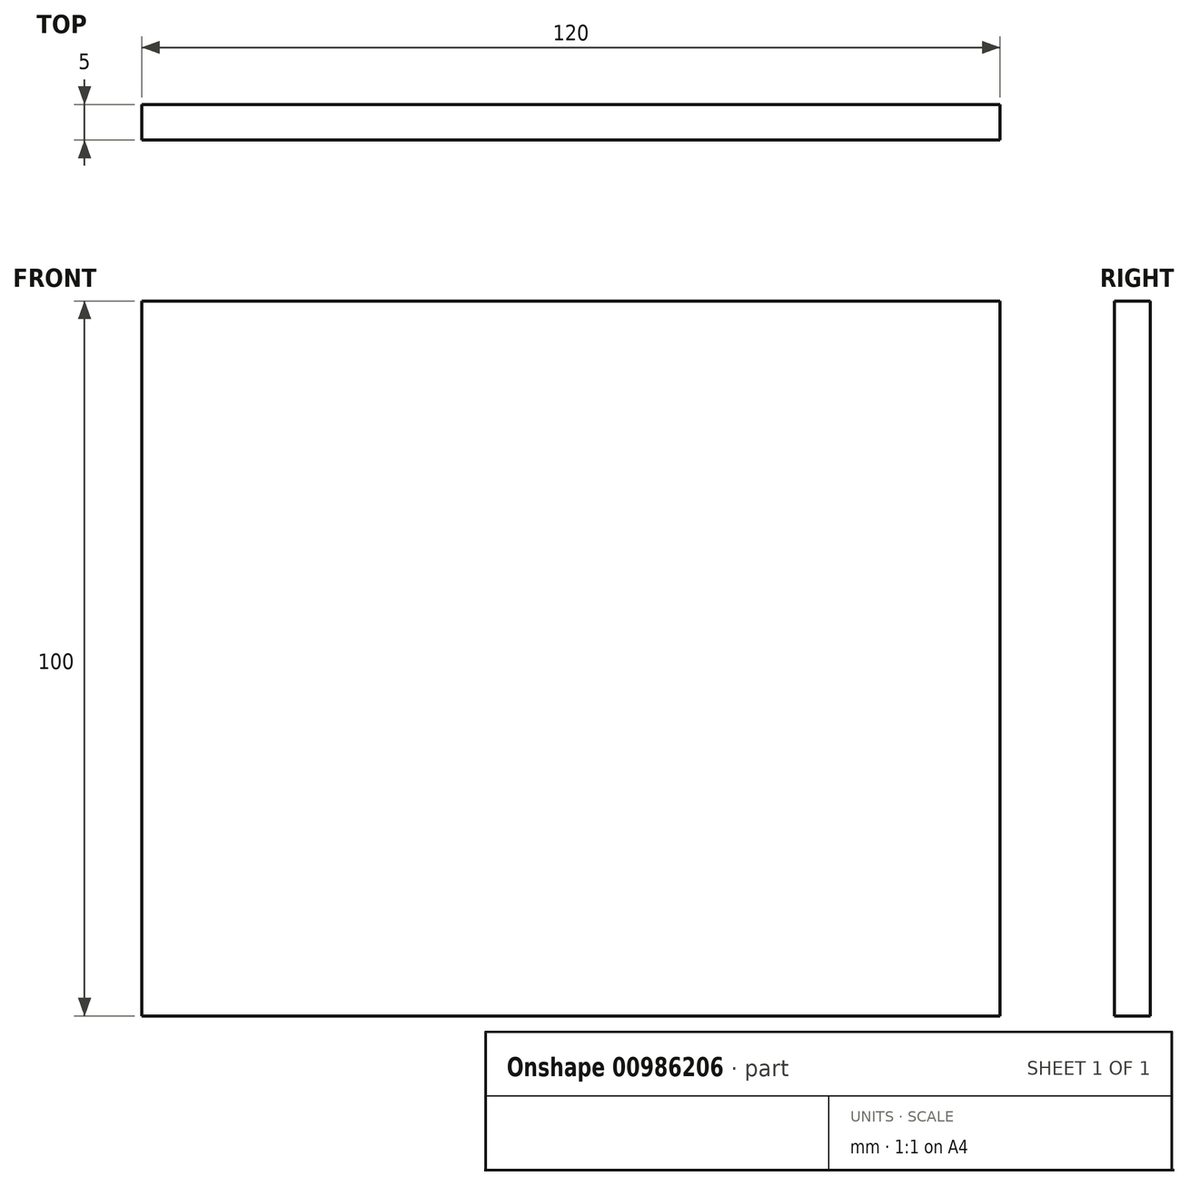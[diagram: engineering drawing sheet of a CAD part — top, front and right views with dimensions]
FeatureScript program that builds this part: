
annotation { "Feature Type Name" : "Feature", "Feature Type Description" : "" }
export const myFeature = defineFeature(function(context is Context, id is Id, definition is map)
    precondition{}
    {
        {
            var Q0;
            Q0=qCreatedBy(makeId("Front.planeOp"),FACE);
            var sketch = newSketch(context, id + "F0", { "sketchPlane" : qUnion([Q0])});
            skLineSegment(sketch, "E0.bottom", {"start": v(-75.65, -20.44) * mm, "end": v(44.35, -20.44) * mm});
            skLineSegment(sketch, "E0.top", {"start": v(-75.65, 79.56) * mm, "end": v(44.35, 79.56) * mm});
            skLineSegment(sketch, "E0.left", {"start": v(-75.65, -20.44) * mm, "end": v(-75.65, 79.56) * mm});
            skLineSegment(sketch, "E0.right", {"start": v(44.35, -20.44) * mm, "end": v(44.35, 79.56) * mm});
            skSolve(sketch);
        }
        {
            var Q0;
            Q0=makeQuery(id+"F0.imprint","IMPRINT",FACE,{"disambiguationData":[TD([[makeQuery(id+"F0.imprint","IMPRINT",EDGE,{"derivedFrom":sQuery(id+"F0.wireOp",EDGE,"E0.bottom")}),1.0]])]});
            extrude(context, id + "F1", {"entities" : qUnion([Q0]), "depth" : 5 * mm, "offsetDistance" : 25 * mm});
        }
    });
